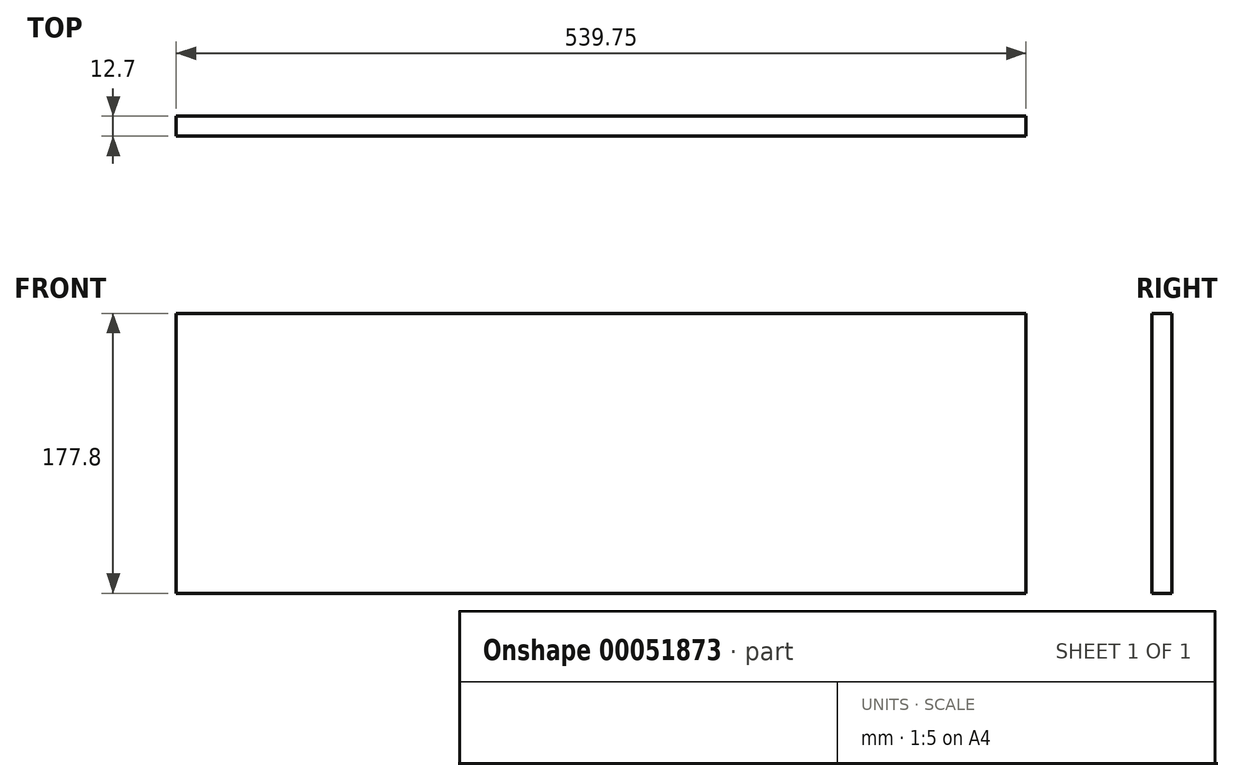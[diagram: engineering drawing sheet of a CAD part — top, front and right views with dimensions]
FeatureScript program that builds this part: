
annotation { "Feature Type Name" : "Feature", "Feature Type Description" : "" }
export const myFeature = defineFeature(function(context is Context, id is Id, definition is map)
    precondition{}
    {
        {
            var Q0;
            Q0=qCreatedBy(makeId("Front.planeOp"),FACE);
            var sketch = newSketch(context, id + "F0", { "sketchPlane" : qUnion([Q0])});
            skLineSegment(sketch, "E0.bottom", {"start": v(-254, 76.2) * mm, "end": v(285.75, 76.2) * mm});
            skLineSegment(sketch, "E0.top", {"start": v(-254, -101.6) * mm, "end": v(285.75, -101.6) * mm});
            skLineSegment(sketch, "E0.left", {"start": v(-254, 76.2) * mm, "end": v(-254, -101.6) * mm});
            skLineSegment(sketch, "E0.right", {"start": v(285.75, 76.2) * mm, "end": v(285.75, -101.6) * mm});
            skSolve(sketch);
        }
        {
            var Q0;
            Q0=makeQuery(id+"F0.imprint","IMPRINT",FACE,{"disambiguationData":[TD([[makeQuery(id+"F0.imprint","IMPRINT",EDGE,{"derivedFrom":sQuery(id+"F0.wireOp",EDGE,"E0.bottom")}),-1.0]])]});
            extrude(context, id + "F1", {"entities" : qUnion([Q0]), "depth" : 12.7 * mm});
        }
    });
